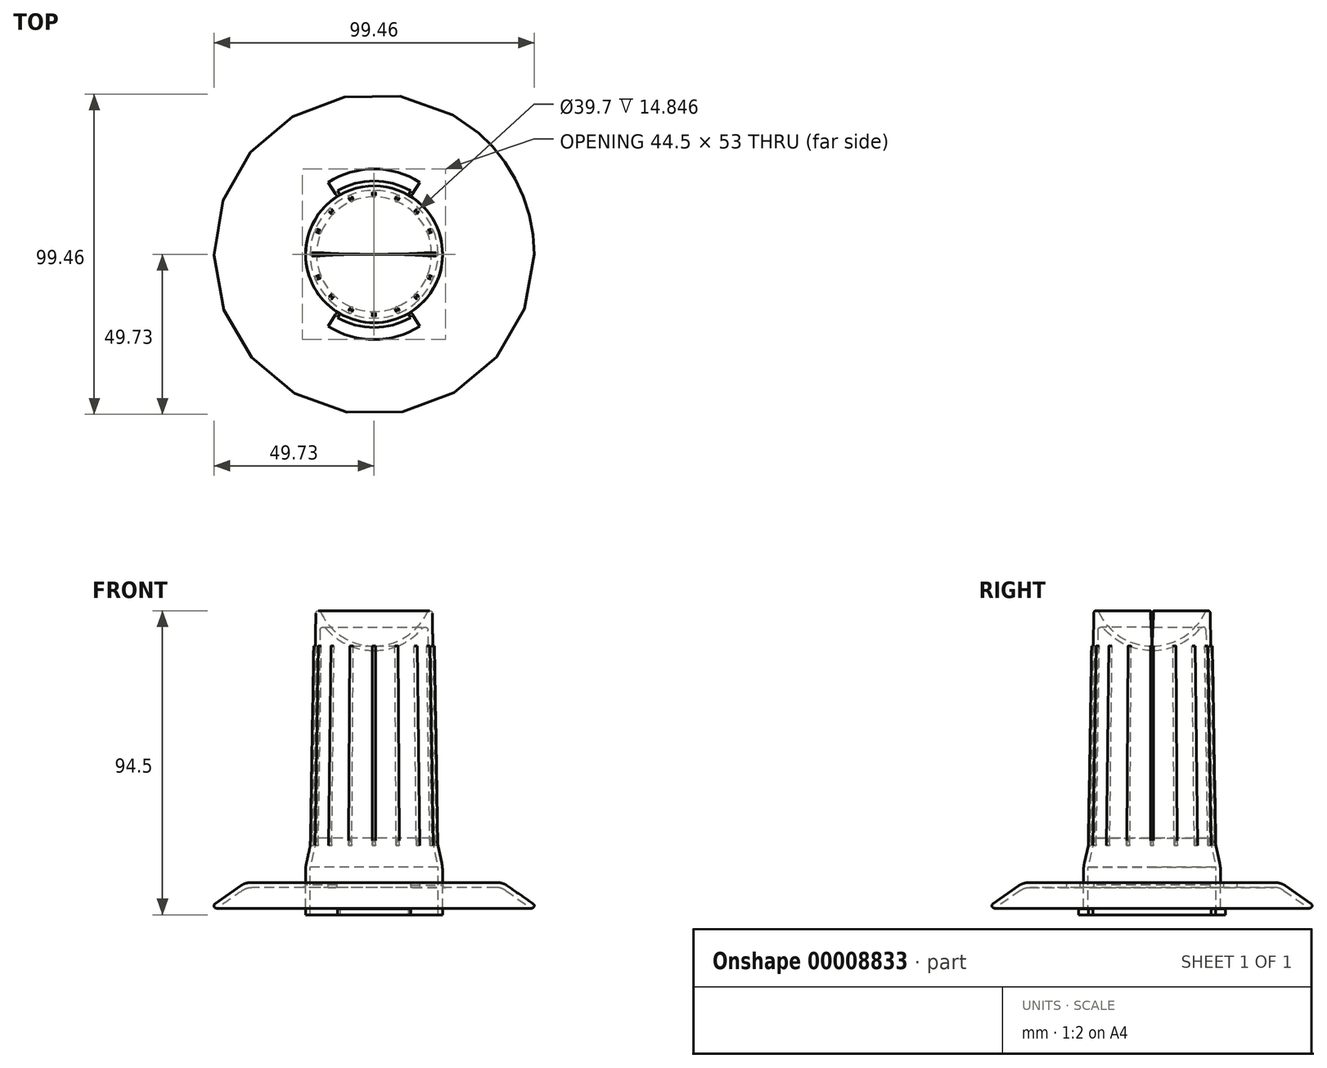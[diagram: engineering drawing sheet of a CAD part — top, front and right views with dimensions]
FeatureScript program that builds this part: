
annotation { "Feature Type Name" : "Feature", "Feature Type Description" : "" }
export const myFeature = defineFeature(function(context is Context, id is Id, definition is map)
    precondition{}
    {
        {
            var Q0;
            Q0=qCreatedBy(makeId("Right.planeOp"),FACE);
            var sketch = newSketch(context, id + "F0", { "sketchPlane" : qUnion([Q0])});
            skLineSegment(sketch, "E0", {"start": v(-18.08, 83.71) * mm, "end": v(-19.25, 14) * mm});
            skLineSegment(sketch, "E1", {"start": v(-19.25, 14) * mm, "end": v(-21.25, 5) * mm});
            skLineSegment(sketch, "E2", {"start": v(-21.25, 5) * mm, "end": v(-21.25, -10) * mm});
            skArc(sketch, "E3", {"start": v(-16.56, 84.04) * mm, "mid": v(-9.81, 76.36) * mm, "end": v(0, 73.5) * mm});
            skLineSegment(sketch, "E4", {"start": v(0, 73.5) * mm, "end": v(0, -10) * mm, "construction": true});
            skLineSegment(sketch, "E5", {"start": v(0, -10) * mm, "end": v(-21.25, -10) * mm, "construction": true});
            skPoint(sketch, "E6.visualSharp", {"position": v(-18, 88.61) * mm});
            skArc(sketch, "E6.filletArc", {"start": v(-16.56, 84.04) * mm, "mid": v(-17.45, 84.48) * mm, "end": v(-18.08, 83.71) * mm});
            skLineSegment(sketch, "E7", {"start": v(0, 84.5) * mm, "end": v(-15.37, 84.5) * mm, "construction": true});
            skLineSegment(sketch, "E8.0", {"start": v(-19.85, 4.85) * mm, "end": v(-19.85, -10) * mm});
            skLineSegment(sketch, "E8.1", {"start": v(-17.85, 13.83) * mm, "end": v(-19.85, 4.85) * mm});
            skLineSegment(sketch, "E8.2", {"start": v(-16.77, 78.42) * mm, "end": v(-17.85, 13.83) * mm});
            skArc(sketch, "E8.3", {"start": v(-15, 79.05) * mm, "mid": v(-8.27, 73.92) * mm, "end": v(0, 72.1) * mm});
            skLineSegment(sketch, "E9", {"start": v(-21.25, -10) * mm, "end": v(-19.85, -10) * mm});
            skLineSegment(sketch, "E10", {"start": v(0, 73.5) * mm, "end": v(0, 72.1) * mm});
            skPoint(sketch, "E11.visualSharp", {"position": v(-16.72, 81.4) * mm});
            skArc(sketch, "E11.filletArc", {"start": v(-15, 79.05) * mm, "mid": v(-16.1, 79.35) * mm, "end": v(-16.77, 78.42) * mm});
            skSolve(sketch);
        }
        {
            var Q0;
            Q0=qCreatedBy(makeId("Right.planeOp"),FACE);
            var sketch = newSketch(context, id + "F1", { "sketchPlane" : qUnion([Q0])});
            skLineSegment(sketch, "E12", {"start": v(-21.25, 0) * mm, "end": v(-40, 0) * mm});
            skLineSegment(sketch, "E13", {"start": v(-40, 0) * mm, "end": v(-50, -7) * mm});
            skLineSegment(sketch, "E14.0", {"start": v(-39.53, -1.5) * mm, "end": v(-49.14, -8.23) * mm});
            skLineSegment(sketch, "E14.1", {"start": v(-21.25, -1.5) * mm, "end": v(-39.53, -1.5) * mm});
            skLineSegment(sketch, "E15", {"start": v(-21.25, 0) * mm, "end": v(-21.25, -1.5) * mm});
            skLineSegment(sketch, "E16", {"start": v(-50, -7) * mm, "end": v(-49.14, -8.23) * mm});
            skSolve(sketch);
        }
        {
            var Q0;
            Q0=qCreatedBy(makeId("Right.planeOp"),FACE);
            var sketch = newSketch(context, id + "F2", { "sketchPlane" : qUnion([Q0])});
            skLineSegment(sketch, "E17", {"start": v(-19.8, 11.57) * mm, "end": v(-18.75, 73.5) * mm});
            skLineSegment(sketch, "E18", {"start": v(-18.75, 73.5) * mm, "end": v(-18.25, 73.5) * mm});
            skLineSegment(sketch, "E19.0", {"start": v(-18.08, 83.71) * mm, "end": v(-19.25, 14) * mm});
            skLineSegment(sketch, "E19.1", {"start": v(-19.25, 14) * mm, "end": v(-19.8, 11.57) * mm});
            skPoint(sketch, "E20.orphan", {"position": v(-21.25, 5) * mm});
            skSolve(sketch);
        }
        {
            var Q0;
            Q0=makeQuery(id+"F0.imprint","IMPRINT",FACE,{"disambiguationData":[TD([[makeQuery(id+"F0.imprint","IMPRINT",EDGE,{"derivedFrom":sQuery(id+"F0.wireOp",EDGE,"E0")}),1.0]])]});
            var Q1;
            Q1=makeQuery(id+"F1.imprint","IMPRINT",FACE,{"disambiguationData":[TD([[makeQuery(id+"F1.imprint","IMPRINT",EDGE,{"derivedFrom":sQuery(id+"F1.wireOp",EDGE,"E12")}),1.0]])]});
            var Q2;
            Q2=sQuery(id+"F0.wireOp",EDGE,"E4");
            revolve(context, id + "F3", {"entities" : qUnion([Q0, Q1]), "axis" : qUnion([Q2]), "revolveType" : RevolveType.FULL});
        }
        {
            var Q0;
            Q0=makeQuery(id+"F2.imprint","IMPRINT",FACE,{"disambiguationData":[TD([[makeQuery(id+"F2.imprint","IMPRINT",EDGE,{"derivedFrom":sQuery(id+"F2.wireOp",EDGE,"E17")}),-1.0]])]});
            var Q1;
            Q1=sQuery(id+"F2.wireOp",EDGE,"E19.0");
            revolve(context, id + "F4", {"entities" : qUnion([Q0]), "axis" : qUnion([Q1]), "revolveType" : RevolveType.FULL});
        }
        {
            var Q0;
            Q0=makeQuery(id+"F4.opRevolve","SWEPT_BODY",BODY,{"disambiguationData":[OSD([sQuery(id+"F2.wireOp",EDGE,"E17"),sQuery(id+"F2.wireOp",EDGE,"E18"),sQuery(id+"F2.wireOp",EDGE,"E19.0"),sQuery(id+"F2.wireOp",EDGE,"E19.1")])]});
            var Q1;
            Q1=sQuery(id+"F0.wireOp",EDGE,"E4");
            circularPattern(context, id + "F5", {"entities" : qUnion([Q0]), "axis" : qUnion([Q1]), "angle" : 360 * degree, "instanceCount" : 16, "equalSpace" : true});
        }
        {
            var Q0;
            Q0=makeQuery(id+"F3.opRevolve","SWEPT_EDGE",EDGE,{"disambiguationData":[OSD([sQuery(id+"F0.wireOp",EDGE,"E1"),sQuery(id+"F0.wireOp",EDGE,"E2")])]});
            var Q1;
            Q1=makeQuery(id+"F3.opRevolve","SWEPT_EDGE",EDGE,{"disambiguationData":[OSD([sQuery(id+"F0.wireOp",EDGE,"E0"),sQuery(id+"F0.wireOp",EDGE,"E1")])]});
            fillet(context, id + "F6", {"entities" : qUnion([Q0, Q1]), "radius" : 10 * mm, "tangentPropagation" : true, "allowEdgeOverflow" : false});
        }
        {
            var Q0;
            Q0=qCreatedBy(makeId("Top.planeOp"),FACE);
            var sketch = newSketch(context, id + "F7", { "sketchPlane" : qUnion([Q0])});
            skArc(sketch, "E21", {"start": v(11.42, 17.92) * mm, "mid": v(0, 21.25) * mm, "end": v(-11.42, 17.92) * mm});
            skArc(sketch, "E22", {"start": v(11.37, 19.7) * mm, "mid": v(0, 22.75) * mm, "end": v(-11.37, 19.7) * mm});
            skArc(sketch, "E23", {"start": v(14.24, 22.35) * mm, "mid": v(0, 26.5) * mm, "end": v(-14.24, 22.35) * mm});
            skLineSegment(sketch, "E24", {"start": v(0, -30) * mm, "end": v(0, 30.3) * mm, "construction": true});
            skLineSegment(sketch, "E25", {"start": v(-14.24, -22.35) * mm, "end": v(-11.42, -17.92) * mm});
            skLineSegment(sketch, "E26.0.MirrorCS", {"start": v(14.24, -22.35) * mm, "end": v(11.42, -17.92) * mm});
            skLineSegment(sketch, "E27", {"start": v(-11.38, -19.7) * mm, "end": v(-10.63, -18.4) * mm});
            skLineSegment(sketch, "E28.0.MirrorCS", {"start": v(11.38, -19.7) * mm, "end": v(10.63, -18.4) * mm});
            skArc(sketch, "E29.trimOffspring", {"start": v(-11.37, -19.7) * mm, "mid": v(0, -22.75) * mm, "end": v(11.37, -19.7) * mm});
            skArc(sketch, "E30.trimOffspring", {"start": v(-14.24, -22.35) * mm, "mid": v(0, -26.5) * mm, "end": v(14.24, -22.35) * mm});
            skLineSegment(sketch, "E31.trimOffspring", {"start": v(11.42, 17.92) * mm, "end": v(14.24, 22.35) * mm});
            skArc(sketch, "E32.trimOffspring", {"start": v(-11.42, -17.92) * mm, "mid": v(0, -21.25) * mm, "end": v(11.42, -17.92) * mm});
            skLineSegment(sketch, "E33.trimOffspring", {"start": v(10.62, 18.4) * mm, "end": v(11.37, 19.7) * mm});
            skLineSegment(sketch, "E34.trimOffspring", {"start": v(-10.62, 18.4) * mm, "end": v(-11.37, 19.7) * mm});
            skLineSegment(sketch, "E35.trimOffspring", {"start": v(-11.42, 17.92) * mm, "end": v(-14.24, 22.35) * mm});
            skSolve(sketch);
        }
        {
            var Q0;
            Q0 = qSketchRegion(id + "F7", true);
            extrude(context, id + "F8", {"entities" : qUnion([Q0]), "operationType" : NewBodyOperationType.REMOVE, "endBound" : BoundingType.UP_TO_NEXT, "oppositeDirection" : true, "depth" : 25 * mm});
        }
        {
            var Q0;
            Q0=makeQuery(id+"F3.opRevolve","SWEPT_FACE",FACE,{"disambiguationData":[OSD([sQuery(id+"F0.wireOp",EDGE,"E9")])]});
            var sketch = newSketch(context, id + "F9", { "sketchPlane" : qUnion([Q0])});
            skArc(sketch, "E36.0.0", {"start": v(-10.62, -18.4) * mm, "mid": v(0, -21.25) * mm, "end": v(10.62, -18.4) * mm});
            skLineSegment(sketch, "E36.0.1", {"start": v(10.62, -18.4) * mm, "end": v(11.37, -19.7) * mm});
            skArc(sketch, "E36.0.2", {"start": v(11.37, -19.7) * mm, "mid": v(0, -22.75) * mm, "end": v(-11.37, -19.7) * mm});
            skLineSegment(sketch, "E36.0.3", {"start": v(-11.37, -19.7) * mm, "end": v(-10.62, -18.4) * mm});
            skLineSegment(sketch, "E36.1.0", {"start": v(-10.63, 18.4) * mm, "end": v(-11.38, 19.7) * mm});
            skArc(sketch, "E36.1.1", {"start": v(-11.37, 19.7) * mm, "mid": v(0, 22.75) * mm, "end": v(11.37, 19.7) * mm});
            skLineSegment(sketch, "E36.1.2", {"start": v(11.38, 19.7) * mm, "end": v(10.63, 18.4) * mm});
            skArc(sketch, "E36.1.3", {"start": v(10.62, 18.4) * mm, "mid": v(0, 21.25) * mm, "end": v(-10.62, 18.4) * mm});
            skSolve(sketch);
        }
        {
            var Q0;
            Q0 = qSketchRegion(id + "F9", true);
            extrude(context, id + "F10", {"entities" : qUnion([Q0]), "operationType" : NewBodyOperationType.ADD, "oppositeDirection" : true, "depth" : 1.8 * mm});
        }
        {
            var Q0;
            Q0=qCreatedBy(makeId("Right.planeOp"),FACE);
            var sketch = newSketch(context, id + "F11", { "sketchPlane" : qUnion([Q0])});
            skLineSegment(sketch, "E37", {"start": v(0.5, 84.5) * mm, "end": v(0, 73.5) * mm});
            skLineSegment(sketch, "E38", {"start": v(0, 73.5) * mm, "end": v(0, 90.28) * mm, "construction": true});
            skLineSegment(sketch, "E39.0.MirrorCS", {"start": v(-0.5, 84.5) * mm, "end": v(0, 73.5) * mm});
            skLineSegment(sketch, "E40", {"start": v(0.5, 84.5) * mm, "end": v(-0.5, 84.5) * mm});
            skSolve(sketch);
        }
        {
            var Q0;
            Q0 = qSketchRegion(id + "F11", true);
            extrude(context, id + "F12", {"entities" : qUnion([Q0]), "operationType" : NewBodyOperationType.REMOVE, "endBound" : BoundingType.THROUGH_ALL, "oppositeDirection" : true, "depth" : 25 * mm, "hasSecondDirection" : true, "secondDirectionBound" : SecondDirectionBoundingType.THROUGH_ALL, "secondDirectionOppositeDirection" : false, "secondDirectionDepth" : 25 * mm});
        }
        {
            var Q0;
            Q0=makeQuery(id+"F3.opRevolve","SWEPT_EDGE",EDGE,{"disambiguationData":[OSD([sQuery(id+"F1.wireOp",EDGE,"E13"),sQuery(id+"F1.wireOp",EDGE,"E16")])]});
            var Q1;
            Q1=makeQuery(id+"F3.opRevolve","SWEPT_EDGE",EDGE,{"disambiguationData":[OSD([sQuery(id+"F1.wireOp",EDGE,"E14.0"),sQuery(id+"F1.wireOp",EDGE,"E16")])]});
            fillet(context, id + "F13", {"entities" : qUnion([Q0, Q1]), "radius" : 0.7 * mm, "tangentPropagation" : true, "allowEdgeOverflow" : false});
        }
        {
            var Q0;
            Q0=makeQuery(id+"F3.opRevolve","SWEPT_EDGE",EDGE,{"disambiguationData":[OSD([sQuery(id+"F1.wireOp",EDGE,"E14.0"),sQuery(id+"F1.wireOp",EDGE,"E14.1")])]});
            var Q1;
            Q1=makeQuery(id+"F3.opRevolve","SWEPT_EDGE",EDGE,{"disambiguationData":[OSD([sQuery(id+"F1.wireOp",EDGE,"E12"),sQuery(id+"F1.wireOp",EDGE,"E13")])]});
            fillet(context, id + "F14", {"entities" : qUnion([Q0, Q1]), "radius" : 5 * mm, "tangentPropagation" : true, "allowEdgeOverflow" : false});
        }
        {
            var Q0;
            {var subQ0=sQuery(id+"F1.wireOp",EDGE,"E14.1");Q0=makeQuery(id+"F8.boolean.opBoolean","SPLIT",EDGE,{"disambiguationData":[TD([makeQuery(id+"F8.opExtrude","SWEPT_FACE",FACE,{"disambiguationData":[OSD([sQuery(id+"F7.wireOp",EDGE,"E25")])]})])],"derivedFrom":makeQuery(id+"F3.opRevolve","SWEPT_EDGE",EDGE,{"disambiguationData":[OSD([subQ0,sQuery(id+"F1.wireOp",EDGE,"E15")])]})});}
            var Q1;
            {var subQ0=sQuery(id+"F1.wireOp",EDGE,"E14.1");Q1=makeQuery(id+"F8.boolean.opBoolean","SPLIT",EDGE,{"disambiguationData":[TD([makeQuery(id+"F8.opExtrude","SWEPT_FACE",FACE,{"disambiguationData":[OSD([sQuery(id+"F7.wireOp",EDGE,"E26.0.MirrorCS")])]})])],"derivedFrom":makeQuery(id+"F3.opRevolve","SWEPT_EDGE",EDGE,{"disambiguationData":[OSD([subQ0,sQuery(id+"F1.wireOp",EDGE,"E15")])]})});}
            var Q2;
            {var subQ0=sQuery(id+"F1.wireOp",EDGE,"E12");Q2=makeQuery(id+"F8.boolean.opBoolean","SPLIT",EDGE,{"disambiguationData":[TD([makeQuery(id+"F8.opExtrude","SWEPT_FACE",FACE,{"disambiguationData":[OSD([sQuery(id+"F7.wireOp",EDGE,"E25")])]})])],"derivedFrom":makeQuery(id+"F3.opRevolve","SWEPT_EDGE",EDGE,{"disambiguationData":[OSD([subQ0,sQuery(id+"F1.wireOp",EDGE,"E15")])]})});}
            var Q3;
            {var subQ0=sQuery(id+"F1.wireOp",EDGE,"E12");Q3=makeQuery(id+"F8.boolean.opBoolean","SPLIT",EDGE,{"disambiguationData":[TD([makeQuery(id+"F8.opExtrude","SWEPT_FACE",FACE,{"disambiguationData":[OSD([sQuery(id+"F7.wireOp",EDGE,"E26.0.MirrorCS")])]})])],"derivedFrom":makeQuery(id+"F3.opRevolve","SWEPT_EDGE",EDGE,{"disambiguationData":[OSD([subQ0,sQuery(id+"F1.wireOp",EDGE,"E15")])]})});}
            fillet(context, id + "F15", {"entities" : qUnion([Q0, Q1, Q2, Q3]), "radius" : 1 * mm, "tangentPropagation" : true, "allowEdgeOverflow" : false});
        }
    });
